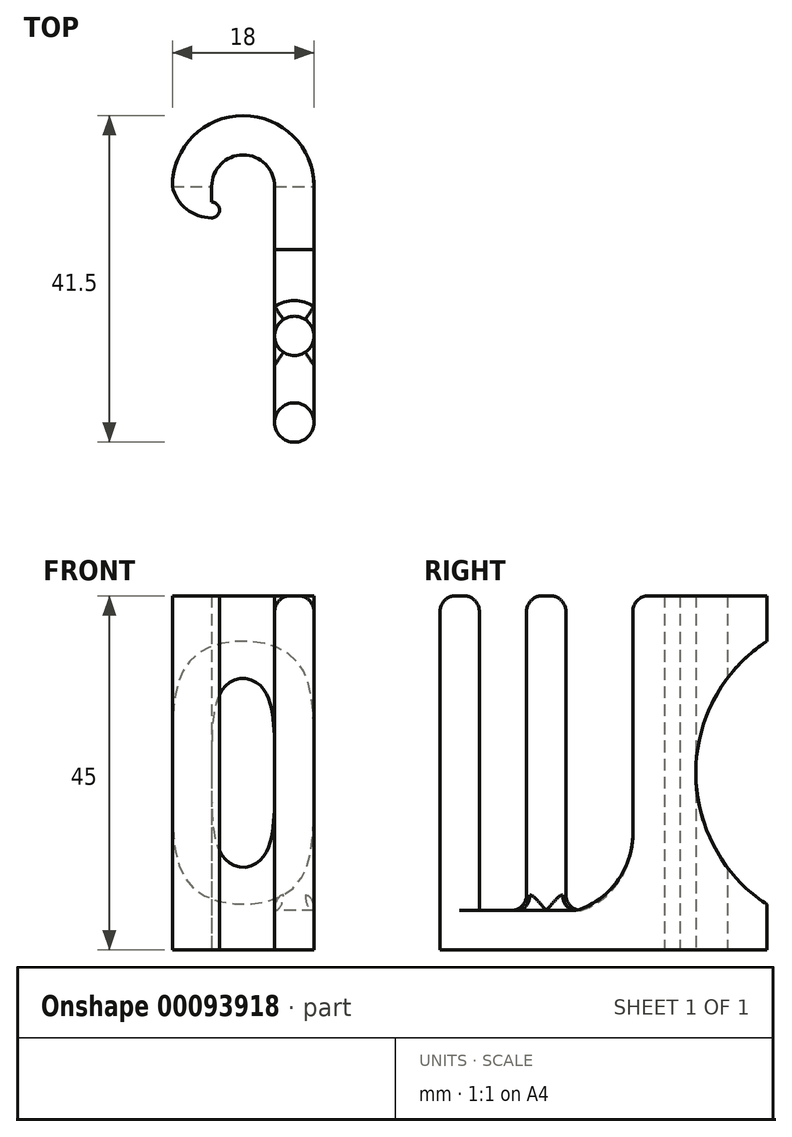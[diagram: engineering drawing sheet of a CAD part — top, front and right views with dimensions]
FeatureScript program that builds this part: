
annotation { "Feature Type Name" : "Feature", "Feature Type Description" : "" }
export const myFeature = defineFeature(function(context is Context, id is Id, definition is map)
    precondition{}
    {
        {
            var Q0;
            Q0=qCreatedBy(makeId("Top.planeOp"),FACE);
            var sketch = newSketch(context, id + "F0", { "sketchPlane" : qUnion([Q0])});
            skLineSegment(sketch, "E0", {"start": v(-4, 0) * mm, "end": v(4, 0) * mm, "construction": true});
            skLineSegment(sketch, "E1", {"start": v(-4, 0) * mm, "end": v(-4, -4) * mm, "construction": true});
            skArc(sketch, "E2", {"start": v(4, 0) * mm, "mid": v(0, 4) * mm, "end": v(-4, 0) * mm});
            skLineSegment(sketch, "E3", {"start": v(-4, -4) * mm, "end": v(-8, -4) * mm, "construction": true});
            skArc(sketch, "E4", {"start": v(9, 0) * mm, "mid": v(0, 9) * mm, "end": v(-9, 0) * mm});
            skLineSegment(sketch, "E5", {"start": v(9, 0) * mm, "end": v(9, -30) * mm});
            skArc(sketch, "E6", {"start": v(4, -30) * mm, "mid": v(6.5, -32.5) * mm, "end": v(9, -30) * mm});
            skLineSegment(sketch, "E7", {"start": v(4, -30) * mm, "end": v(9, -30) * mm, "construction": true});
            skArc(sketch, "E8", {"start": v(-4, -4) * mm, "mid": v(-3, -3) * mm, "end": v(-4, -2) * mm});
            skLineSegment(sketch, "E9", {"start": v(-4, -2) * mm, "end": v(-4, 0) * mm});
            skArc(sketch, "E10", {"start": v(-9, 0) * mm, "mid": v(-7.2, -2.88) * mm, "end": v(-4, -4) * mm});
            skLineSegment(sketch, "E11", {"start": v(4, 0) * mm, "end": v(4, -30) * mm});
            skSolve(sketch);
        }
        {
            var Q0;
            Q0 = qSketchRegion(id + "F0", true);
            extrude(context, id + "F1", {"entities" : qUnion([Q0]), "depth" : 5 * mm});
        }
        {
            var Q0;
            Q0=makeQuery(id+"F1.opExtrude","CAP_FACE",FACE,{"disambiguationData":[OSD([sQuery(id+"F0.wireOp",EDGE,"E1"),sQuery(id+"F0.wireOp",EDGE,"FUjUHcG7-UrtA-xhsf-RJNG-7LBNOInVULmC"),sQuery(id+"F0.wireOp",EDGE,"E2"),sQuery(id+"F0.wireOp",EDGE,"PLliaCrf-zDIH-ePHJ-L58h-8VDLheSJXvMW"),sQuery(id+"F0.wireOp",EDGE,"o6JoGevt-oOAn-gUFO-Z36Q-bU6nzk2KqRE1"),sQuery(id+"F0.wireOp",EDGE,"E4"),sQuery(id+"F0.wireOp",EDGE,"E5"),sQuery(id+"F0.wireOp",EDGE,"E6"),sQuery(id+"F0.wireOp",EDGE,"oqys9VUr-H5Cx-NeNL-nwoW-YLmbEKvUMedX"),sQuery(id+"F0.wireOp",EDGE,"kYl1BZvq-8JEG-mwsc-4GBF-ZrzKpucVIevD"),sQuery(id+"F0.wireOp",EDGE,"WnGeUwyx-kRIj-0WaU-Dm0x-UqIITiZ0Iud9")])],"isStart":false});
            var sketch = newSketch(context, id + "F2", { "sketchPlane" : qUnion([Q0])});
            skArc(sketch, "E12.0", {"start": v(9, 0) * mm, "mid": v(0, 9) * mm, "end": v(-9, 0) * mm});
            skArc(sketch, "E13.0", {"start": v(4, 0) * mm, "mid": v(0, 4) * mm, "end": v(-4, 0) * mm});
            skLineSegment(sketch, "E14.0", {"start": v(4, 0) * mm, "end": v(4, -8) * mm});
            skLineSegment(sketch, "E15.0", {"start": v(9, -30) * mm, "end": v(9, -30) * mm});
            skLineSegment(sketch, "E16", {"start": v(9, 0) * mm, "end": v(9, -8) * mm});
            skLineSegment(sketch, "E17", {"start": v(4, -8) * mm, "end": v(9, -8) * mm});
            skLineSegment(sketch, "E18.0", {"start": v(-4, -2) * mm, "end": v(-4, 0) * mm});
            skArc(sketch, "E19.0", {"start": v(-4, -4) * mm, "mid": v(-3, -3) * mm, "end": v(-4, -2) * mm});
            skArc(sketch, "E20.0", {"start": v(-9, 0) * mm, "mid": v(-7.2, -2.88) * mm, "end": v(-4, -4) * mm});
            skLineSegment(sketch, "E21", {"start": v(6.5, -8) * mm, "end": v(6.5, -30) * mm, "construction": true});
            skCircle(sketch, "E22", {"center": v(6.5, -19) * mm, "radius": 2.5 * mm});
            skCircle(sketch, "E23", {"center": v(6.5, -30) * mm, "radius": 2.5 * mm});
            skSolve(sketch);
        }
        {
            var Q0;
            Q0 = qSketchRegion(id + "F2", true);
            extrude(context, id + "F3", {"entities" : qUnion([Q0]), "operationType" : NewBodyOperationType.ADD, "depth" : 40 * mm});
        }
        {
            var Q0;
            Q0=makeQuery(id+"F3.opExtrude","CAP_FACE",FACE,{"disambiguationData":[OSD([sQuery(id+"F2.wireOp",EDGE,"E22")])],"isStart":false});
            var Q1;
            Q1=makeQuery(id+"F3.opExtrude","CAP_FACE",FACE,{"disambiguationData":[OSD([sQuery(id+"F2.wireOp",EDGE,"E23")])],"isStart":false});
            var Q2;
            Q2=makeQuery(id+"F3.opExtrude","CAP_EDGE",EDGE,{"disambiguationData":[OSD([sQuery(id+"F2.wireOp",EDGE,"E17")])],"isStart":false});
            var Q3;
            Q3=makeQuery(id+"F3.opExtrude","CAP_EDGE",EDGE,{"disambiguationData":[OSD([sQuery(id+"F2.wireOp",EDGE,"E23")])],"isStart":true});
            var Q4;
            Q4=makeQuery(id+"F3.boolean.opBoolean","SPLIT",EDGE,{"disambiguationData":[OD(1.0)],"derivedFrom":makeQuery(id+"F3.opExtrude","CAP_EDGE",EDGE,{"disambiguationData":[OSD([sQuery(id+"F2.wireOp",EDGE,"E22")])],"isStart":true})});
            fillet(context, id + "F4", {"entities" : qUnion([Q0, Q1, Q2, Q3, Q4]), "radius" : 2 * mm, "tangentPropagation" : true, "allowEdgeOverflow" : false});
        }
        {
            var Q0;
            Q0=makeQuery(id+"F3.opExtrude","CAP_EDGE",EDGE,{"disambiguationData":[OSD([sQuery(id+"F2.wireOp",EDGE,"E17")])],"isStart":true});
            fillet(context, id + "F5", {"entities" : qUnion([Q0]), "radius" : 10 * mm, "tangentPropagation" : true, "allowEdgeOverflow" : false});
        }
        {
            var Q0;
            Q0=qCreatedBy(makeId("Right.planeOp"),FACE);
            var sketch = newSketch(context, id + "F6", { "sketchPlane" : qUnion([Q0])});
            skLineSegment(sketch, "E24.0", {"start": v(0, 45) * mm, "end": v(0, 0) * mm, "construction": true});
            skLineSegment(sketch, "E25", {"start": v(9, 45) * mm, "end": v(9, 0) * mm, "construction": true});
            skLineSegment(sketch, "E26", {"start": v(0, 22.5) * mm, "end": v(20, 22.5) * mm, "construction": true});
            skLineSegment(sketch, "E27", {"start": v(20, 42.5) * mm, "end": v(20, 2.5) * mm});
            skArc(sketch, "E28", {"start": v(20, 42.5) * mm, "mid": v(0, 22.5) * mm, "end": v(20, 2.5) * mm});
            skSolve(sketch);
        }
        {
            var Q0;
            Q0 = qSketchRegion(id + "F6", true);
            extrude(context, id + "F7", {"entities" : qUnion([Q0]), "operationType" : NewBodyOperationType.REMOVE, "endBound" : BoundingType.THROUGH_ALL, "oppositeDirection" : true, "depth" : 25 * mm, "hasSecondDirection" : true, "secondDirectionBound" : SecondDirectionBoundingType.THROUGH_ALL, "secondDirectionOppositeDirection" : false, "secondDirectionDepth" : 25 * mm});
        }
    });
